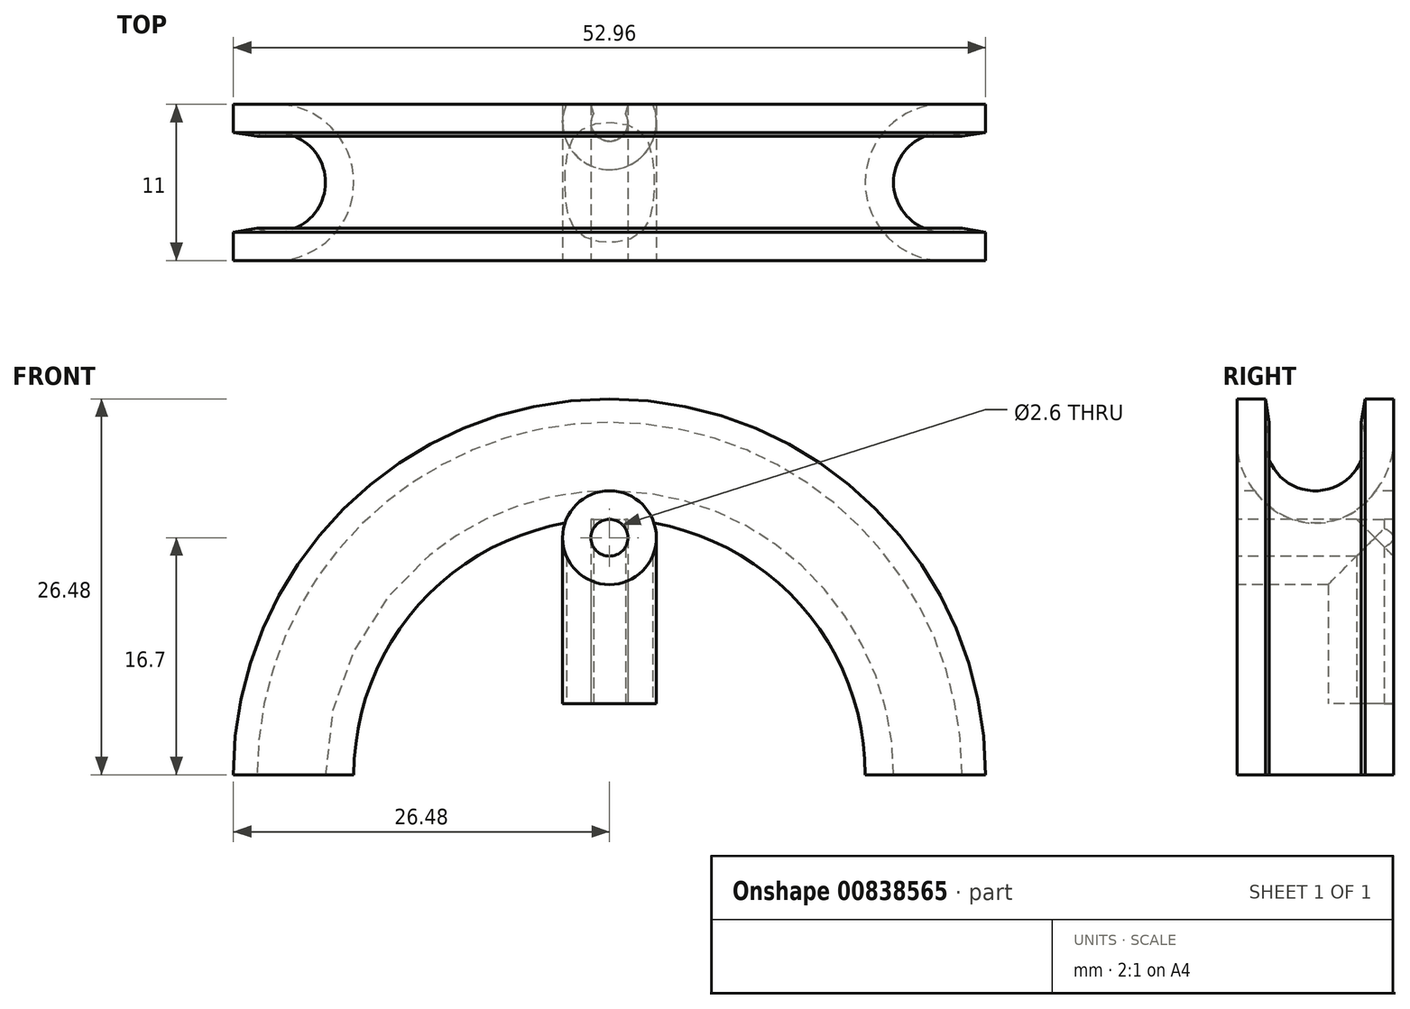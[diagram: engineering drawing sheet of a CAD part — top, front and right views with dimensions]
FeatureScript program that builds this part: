
annotation { "Feature Type Name" : "Feature", "Feature Type Description" : "" }
export const myFeature = defineFeature(function(context is Context, id is Id, definition is map)
    precondition{}
    {
        {
            assignVariable(context, id + "F0", {"name" : "cableDiameter", "lengthValue" : 7 * mm, "variableType" : VariableType.LENGTH});
        }
        {
            assignVariable(context, id + "F1", {"variableType" : VariableType.LENGTH, "name" : "guideRadius", "lengthValue" : 20 * mm});
        }
        {
            assignVariable(context, id + "F2", {"variableType" : VariableType.LENGTH, "name" : "wallThickness", "lengthValue" : 2 * mm});
        }
        {
            assignVariable(context, id + "F3", {"variableType" : VariableType.LENGTH, "name" : "supportDiameter", "lengthValue" : 2.6 * mm});
        }
        {
            assignVariable(context, id + "F4", {"variableType" : VariableType.LENGTH, "name" : "supportWidth", "lengthValue" : 11 * mm});
        }
        {
            var Q0;
            Q0=qCreatedBy(makeId("Front.planeOp"),FACE);
            var sketch = newSketch(context, id + "F5", { "sketchPlane" : qUnion([Q0])});
            skArc(sketch, "E0", {"start": v(20, 0) * mm, "mid": v(0, 20) * mm, "end": v(-20, 0) * mm});
            skSolve(sketch);
        }
        {
            var Q0;
            Q0=qCreatedBy(makeId("Top.planeOp"),FACE);
            var sketch = newSketch(context, id + "F6", { "sketchPlane" : qUnion([Q0])});
            skCircle(sketch, "E1", {"center": v(23.5, 0) * mm, "radius": 3.5 * mm});
            skPoint(sketch, "E2", {"position": v(20, 0) * mm});
            skCircle(sketch, "E3.0", {"center": v(23.5, 0) * mm, "radius": 5.5 * mm});
            skLineSegment(sketch, "E4", {"start": v(23.48, 5.5) * mm, "end": v(23.48, -5.5) * mm, "construction": true});
            skLineSegment(sketch, "E5", {"start": v(23.48, 5.5) * mm, "end": v(26.48, 5.5) * mm});
            skLineSegment(sketch, "E6", {"start": v(26.48, 5.5) * mm, "end": v(26.48, -5.5) * mm});
            skLineSegment(sketch, "E7", {"start": v(26.48, -5.5) * mm, "end": v(23.48, -5.5) * mm});
            skLineSegment(sketch, "E8", {"start": v(23.48, 3.5) * mm, "end": v(26.48, 3.5) * mm, "construction": true});
            skLineSegment(sketch, "E9", {"start": v(23.48, -3.5) * mm, "end": v(26.48, -3.5) * mm, "construction": true});
            skCircle(sketch, "E10", {"center": v(0, 4.2) * mm, "radius": 1.3 * mm});
            skCircle(sketch, "E11.0", {"center": v(0, 4.2) * mm, "radius": 0.9 * mm, "construction": true});
            skCircle(sketch, "E12.0", {"center": v(0, 4.2) * mm, "radius": 3.3 * mm});
            skLineSegment(sketch, "E13", {"start": v(1.3, 4.2) * mm, "end": v(1.3, 7.23) * mm, "construction": true});
            skLineSegment(sketch, "E14", {"start": v(-1.3, 4.2) * mm, "end": v(-1.3, 7.23) * mm, "construction": true});
            skCircle(sketch, "E15.0", {"center": v(23.5, 0) * mm, "radius": 3 * mm, "construction": true});
            skLineSegment(sketch, "E16", {"start": v(26.48, 3.5) * mm, "end": v(24.82, 3.24) * mm});
            skLineSegment(sketch, "E17", {"start": v(26.48, -3.5) * mm, "end": v(24.82, -3.24) * mm});
            skLineSegment(sketch, "E18", {"start": v(0, 0) * mm, "end": v(0, 5.5) * mm, "construction": true});
            skLineSegment(sketch, "E19", {"start": v(23.48, 5.5) * mm, "end": v(-3.03, 5.5) * mm});
            skLineSegment(sketch, "E20", {"start": v(1.3, 5.5) * mm, "end": v(1.12, 4.86) * mm});
            skLineSegment(sketch, "E21", {"start": v(1.12, 4.86) * mm, "end": v(-1.12, 4.86) * mm, "construction": true});
            skLineSegment(sketch, "E22", {"start": v(-1.12, 4.86) * mm, "end": v(-1.3, 5.5) * mm});
            skSolve(sketch);
        }
        {
            var Q0;
            {var subQ6=sQuery(id+"F6.wireOp",EDGE,"E16");Q0=makeQuery(id+"F6.imprint","IMPRINT",FACE,{"disambiguationData":[TD([[makeQuery(id+"F6.imprint","IMPRINT",EDGE,{"derivedFrom":subQ6}),-1.0]])]});}
            var Q1;
            {var subQ0=sQuery(id+"F6.wireOp",EDGE,"E7");Q1=makeQuery(id+"F6.imprint","IMPRINT",FACE,{"disambiguationData":[TD([[makeQuery(id+"F6.imprint","IMPRINT",EDGE,{"derivedFrom":subQ0}),-1.0]])]});}
            var Q2;
            {var subQ0=sQuery(id+"F6.wireOp",EDGE,"E5");Q2=makeQuery(id+"F6.imprint","IMPRINT",FACE,{"disambiguationData":[TD([[makeQuery(id+"F6.imprint","IMPRINT",EDGE,{"derivedFrom":subQ0}),-1.0]])]});}
            var Q3;
            Q3=sQuery(id+"F5.wireOp",EDGE,"E0");
            sweep(context, id + "F7", {"profiles" : qUnion([Q0, Q1, Q2]), "path" : qUnion([Q3])});
        }
        {
            var Q0;
            Q0=qCreatedBy(makeId("Front.planeOp"),FACE);
            var sketch = newSketch(context, id + "F8", { "sketchPlane" : qUnion([Q0])});
            skCircle(sketch, "E23", {"center": v(0, 16.7) * mm, "radius": 1.3 * mm});
            skLineSegment(sketch, "E24", {"start": v(0, 15.4) * mm, "end": v(0, 0) * mm, "construction": true});
            skCircle(sketch, "E25.0", {"center": v(0, 16.7) * mm, "radius": 3.3 * mm});
            skSolve(sketch);
        }
        {
            var Q0;
            Q0 = qSketchRegion(id + "F8", true);
            extrude(context, id + "F9", {"entities" : qUnion([Q0]), "operationType" : NewBodyOperationType.ADD, "endBound" : BoundingType.SYMMETRIC, "oppositeDirection" : true, "depth" : getVariable(context, 'supportWidth'), "offsetDistance" : 25 * mm, "hasSecondDirection" : true, "secondDirectionOppositeDirection" : false, "secondDirectionDepth" : getVariable(context, 'cableDiameter') / 2});
        }
        {
            var Q0;
            {var subQ5=sQuery(id+"F6.wireOp",EDGE,"E20");Q0=makeQuery(id+"F6.imprint","IMPRINT",FACE,{"disambiguationData":[TD([[makeQuery(id+"F6.imprint","IMPRINT",EDGE,{"derivedFrom":subQ5}),1.0]])]});}
            extrude(context, id + "F10", {"entities" : qUnion([Q0]), "operationType" : NewBodyOperationType.ADD, "depth" : getVariable(context, 'guideRadius') - getVariable(context, 'wallThickness') - (getVariable(context, 'supportDiameter') / 2), "offsetDistance" : 25 * mm, "hasSecondDirection" : true, "secondDirectionOppositeDirection" : true, "secondDirectionDepth" : -5 * mm});
        }
        {
            var Q0;
            {var subQ0=sQuery(id+"F6.wireOp",EDGE,"E10");var subQ1=makeQuery(id+"F6.imprint","INTERSECT",VERTEX,{"derivedFrom":[subQ0,sQuery(id+"F6.wireOp",EDGE,"E20")]});Q0=makeQuery(id+"F6.imprint","IMPRINT",FACE,{"disambiguationData":[TD([[makeQuery(id+"F6.imprint","IMPRINT",EDGE,{"disambiguationData":[TD([[subQ1,-1.0]])],"derivedFrom":subQ0}),1.0]])]});}
            var Q1;
            {var subQ0=sQuery(id+"F6.wireOp",EDGE,"E20");Q1=makeQuery(id+"F6.imprint","IMPRINT",FACE,{"disambiguationData":[TD([[makeQuery(id+"F6.imprint","IMPRINT",EDGE,{"derivedFrom":subQ0}),-1.0]])]});}
            var Q2;
            {var subQ0=sQuery(id+"F6.wireOp",EDGE,"E22");Q2=makeQuery(id+"F6.imprint","IMPRINT",FACE,{"disambiguationData":[TD([[makeQuery(id+"F6.imprint","IMPRINT",EDGE,{"derivedFrom":subQ0}),-1.0]])]});}
            var Q3;
            {var subQ0=sQuery(id+"F6.wireOp",EDGE,"E19");var subQ4=sQuery(id+"F6.wireOp",EDGE,"E10");var subQ5=makeQuery(id+"F6.imprint","INTERSECT",VERTEX,{"disambiguationData":[OD(0.0)],"derivedFrom":[subQ4,subQ0]});Q3=makeQuery(id+"F6.imprint","IMPRINT",FACE,{"disambiguationData":[TD([[makeQuery(id+"F6.imprint","IMPRINT",EDGE,{"disambiguationData":[TD([[subQ5,-1.0]])],"derivedFrom":subQ4}),-1.0]])]});}
            extrude(context, id + "F11", {"entities" : qUnion([Q0, Q1, Q2, Q3]), "operationType" : NewBodyOperationType.REMOVE, "depth" : getVariable(context, 'guideRadius') - getVariable(context, 'wallThickness'), "offsetDistance" : 25 * mm});
        }
        {
            var Q0;
            Q0=makeQuery(id+"F8.imprint","IMPRINT",FACE,{"disambiguationData":[TD([[makeQuery(id+"F8.imprint","IMPRINT",EDGE,{"derivedFrom":sQuery(id+"F8.wireOp",EDGE,"E23")}),1.0]])]});
            extrude(context, id + "F12", {"entities" : qUnion([Q0]), "operationType" : NewBodyOperationType.REMOVE, "endBound" : BoundingType.SYMMETRIC, "oppositeDirection" : true, "depth" : getVariable(context, 'supportWidth'), "offsetDistance" : 25 * mm});
        }
    });
